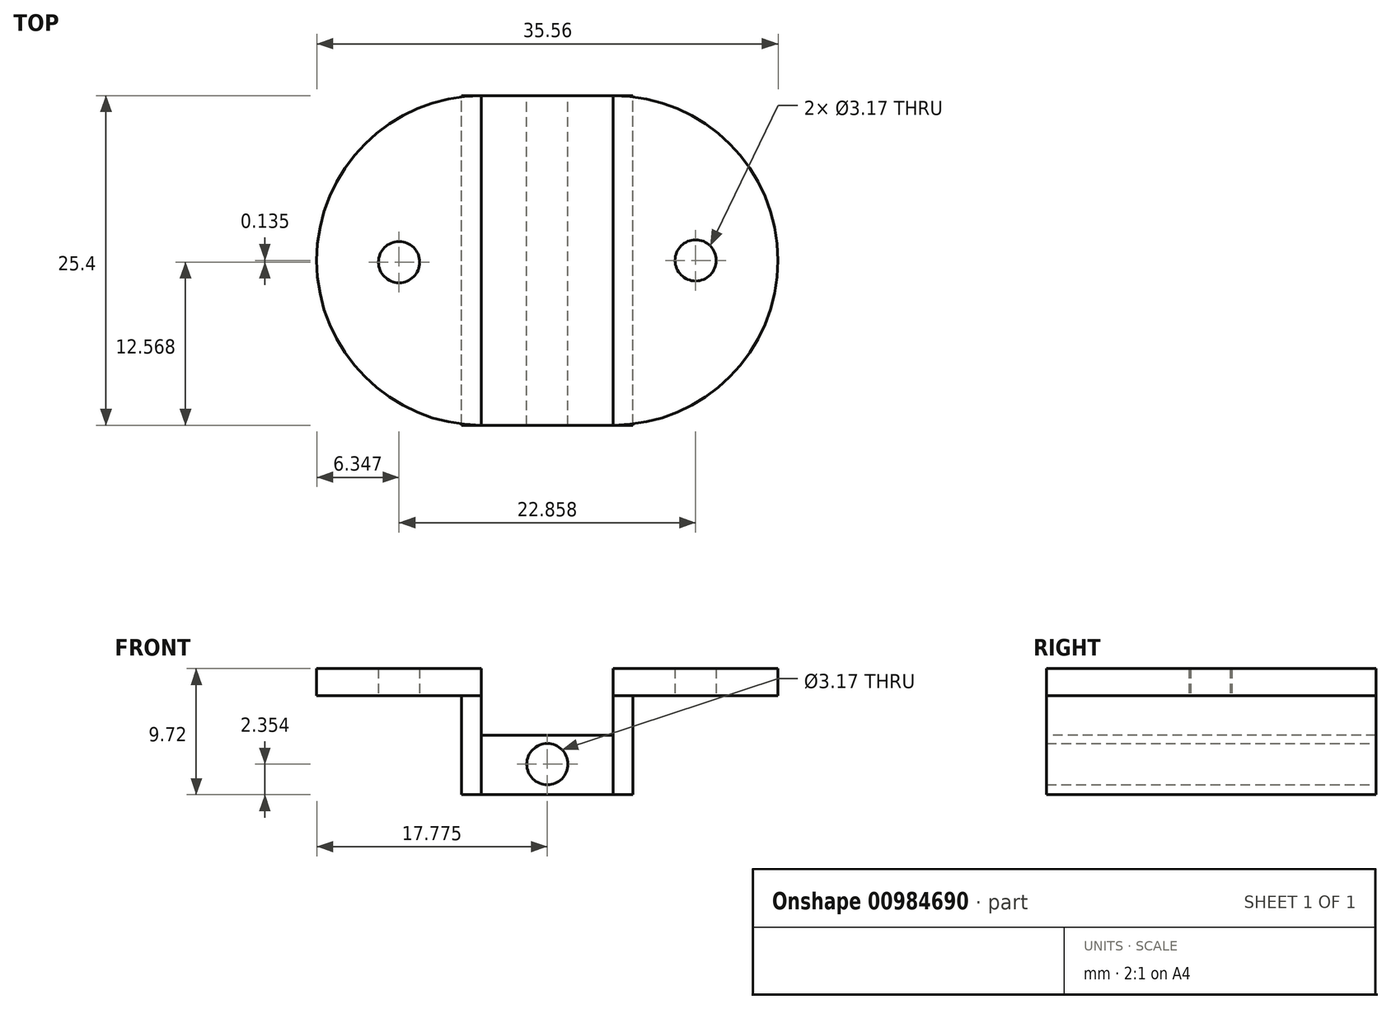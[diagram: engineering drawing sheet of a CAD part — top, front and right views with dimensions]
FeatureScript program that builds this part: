
annotation { "Feature Type Name" : "Feature", "Feature Type Description" : "" }
export const myFeature = defineFeature(function(context is Context, id is Id, definition is map)
    precondition{}
    {
        {
            var Q0;
            Q0=qCreatedBy(makeId("Top.planeOp"),FACE);
            var sketch = newSketch(context, id + "F0", { "sketchPlane" : qUnion([Q0])});
            skLineSegment(sketch, "E0", {"start": v(-48.3, 33.5) * mm, "end": v(-48.3, 8.1) * mm});
            skLineSegment(sketch, "E1", {"start": v(-48.3, 8.1) * mm, "end": v(-48.3, 33.5) * mm});
            skLineSegment(sketch, "E2", {"start": v(-48.3, 33.5) * mm, "end": v(-38.13, 33.5) * mm});
            skLineSegment(sketch, "E3", {"start": v(-38.13, 8.1) * mm, "end": v(-48.3, 8.1) * mm});
            skLineSegment(sketch, "E4", {"start": v(-38.13, 8.1) * mm, "end": v(-38.13, 33.5) * mm});
            skLineSegment(sketch, "E5.bottom", {"start": v(-38.13, 33.5) * mm, "end": v(-36.61, 33.5) * mm});
            skLineSegment(sketch, "E5.top", {"start": v(-38.13, 33.5) * mm, "end": v(-36.61, 33.5) * mm});
            skLineSegment(sketch, "E5.left", {"start": v(-38.13, 33.5) * mm, "end": v(-38.13, 33.5) * mm});
            skLineSegment(sketch, "E5.right", {"start": v(-36.61, 33.5) * mm, "end": v(-36.61, 33.5) * mm});
            skLineSegment(sketch, "E6.bottom", {"start": v(-38.13, 8.1) * mm, "end": v(-36.61, 8.1) * mm});
            skLineSegment(sketch, "E7", {"start": v(-48.3, 33.5) * mm, "end": v(-49.82, 33.5) * mm});
            skLineSegment(sketch, "E8", {"start": v(-48.3, 8.1) * mm, "end": v(-49.82, 8.1) * mm});
            skLineSegment(sketch, "E9", {"start": v(-49.82, 8.1) * mm, "end": v(-49.82, 33.5) * mm});
            skLineSegment(sketch, "E10", {"start": v(-36.61, 8.1) * mm, "end": v(-36.61, 33.5) * mm});
            skLineSegment(sketch, "E11.bottom", {"start": v(-36.61, 8.1) * mm, "end": v(-38.13, 8.1) * mm});
            skLineSegment(sketch, "E11.top", {"start": v(-36.61, 33.5) * mm, "end": v(-38.13, 33.5) * mm});
            skLineSegment(sketch, "E12.bottom", {"start": v(-48.3, 8.1) * mm, "end": v(-38.03, 8.1) * mm});
            skLineSegment(sketch, "E13.bottom", {"start": v(-36.61, 33.5) * mm, "end": v(-21.77, 33.5) * mm});
            skLineSegment(sketch, "E13.top", {"start": v(-36.61, 33.5) * mm, "end": v(-21.77, 33.5) * mm});
            skLineSegment(sketch, "E13.right", {"start": v(-21.77, 33.5) * mm, "end": v(-21.77, 33.5) * mm});
            skLineSegment(sketch, "E14.bottom", {"start": v(-36.61, 8.1) * mm, "end": v(-21.77, 8.1) * mm});
            skLineSegment(sketch, "E14.top", {"start": v(-36.61, 8.1) * mm, "end": v(-21.77, 8.1) * mm});
            skLineSegment(sketch, "E14.left", {"start": v(-36.61, 8.1) * mm, "end": v(-36.61, 8.1) * mm});
            skLineSegment(sketch, "E14.right", {"start": v(-21.77, 8.1) * mm, "end": v(-21.77, 8.1) * mm});
            skLineSegment(sketch, "E15.bottom", {"start": v(-49.82, 8.1) * mm, "end": v(-64.66, 8.1) * mm});
            skLineSegment(sketch, "E15.top", {"start": v(-49.82, 8.1) * mm, "end": v(-64.66, 8.1) * mm});
            skLineSegment(sketch, "E15.left", {"start": v(-49.82, 8.1) * mm, "end": v(-49.82, 8.1) * mm});
            skLineSegment(sketch, "E15.right", {"start": v(-64.66, 8.1) * mm, "end": v(-64.66, 8.1) * mm});
            skLineSegment(sketch, "E16.bottom", {"start": v(-49.82, 33.5) * mm, "end": v(-64.66, 33.5) * mm});
            skLineSegment(sketch, "E16.top", {"start": v(-49.82, 33.5) * mm, "end": v(-64.66, 33.5) * mm});
            skLineSegment(sketch, "E16.left", {"start": v(-49.82, 33.5) * mm, "end": v(-49.82, 33.5) * mm});
            skLineSegment(sketch, "E16.right", {"start": v(-64.66, 33.5) * mm, "end": v(-64.66, 33.5) * mm});
            skLineSegment(sketch, "E17", {"start": v(-64.66, 33.5) * mm, "end": v(-64.66, 8.1) * mm});
            skLineSegment(sketch, "E18", {"start": v(-21.77, 33.5) * mm, "end": v(-21.77, 8.1) * mm});
            skSolve(sketch);
        }
        {
            var Q0;
            Q0=qCreatedBy(makeId("Front.planeOp"),FACE);
            var sketch = newSketch(context, id + "F1", { "sketchPlane" : qUnion([Q0])});
            skSolve(sketch);
        }
        {
            var Q0;
            Q0=makeQuery(id+"F0.imprint","IMPRINT",FACE,{"disambiguationData":[TD([[makeQuery(id+"F0.imprint","IMPRINT",EDGE,{"derivedFrom":sQuery(id+"F0.wireOp",EDGE,"E0")}),1.0]])]});
            extrude(context, id + "F2", {"entities" : qUnion([Q0]), "depth" : 4.57 * mm, "offsetDistance" : 25.4 * mm});
        }
        {
            var Q0;
            Q0=qSketchRegion(id+"F1",true);
            var Q1;
            {var subQ1=sQuery(id+"F0.wireOp",EDGE,"E4");Q1=makeQuery(id+"F0.imprint","IMPRINT",FACE,{"disambiguationData":[TD([[makeQuery(id+"F0.imprint","IMPRINT",EDGE,{"derivedFrom":subQ1}),-1.0]])]});}
            var Q2;
            Q2=makeQuery(id+"F0.imprint","IMPRINT",FACE,{"disambiguationData":[TD([[makeQuery(id+"F0.imprint","IMPRINT",EDGE,{"derivedFrom":sQuery(id+"F0.wireOp",EDGE,"E0")}),-1.0]])]});
            extrude(context, id + "F3", {"entities" : qUnion([Q0, Q1, Q2]), "depth" : 7.62 * mm, "offsetDistance" : 25.4 * mm});
        }
        {
            var Q0;
            Q0=makeQuery(id+"F3.opExtrude","CAP_FACE",FACE,{"disambiguationData":[OSD([sQuery(id+"F0.wireOp",EDGE,"E0"),sQuery(id+"F0.wireOp",EDGE,"E7"),sQuery(id+"F0.wireOp",EDGE,"E8"),sQuery(id+"F0.wireOp",EDGE,"E9")])],"isStart":false});
            var sketch = newSketch(context, id + "F4", { "sketchPlane" : qUnion([Q0])});
            skArc(sketch, "E19", {"start": v(-48.3, 33.5) * mm, "mid": v(-61, 20.8) * mm, "end": v(-48.3, 8.1) * mm});
            skCircle(sketch, "E20", {"center": v(-54.64, 20.67) * mm, "radius": 1.59 * mm});
            skPoint(sketch, "E20.centerSnap0", {"position": v(-59.55, 20.67) * mm});
            skSolve(sketch);
        }
        {
            var Q0;
            Q0=makeQuery(id+"F3.opExtrude","CAP_FACE",FACE,{"disambiguationData":[OSD([sQuery(id+"F0.wireOp",EDGE,"E4"),sQuery(id+"F0.wireOp",EDGE,"E5.bottom"),sQuery(id+"F0.wireOp",EDGE,"E6.bottom"),sQuery(id+"F0.wireOp",EDGE,"E10")])],"isStart":false});
            var sketch = newSketch(context, id + "F5", { "sketchPlane" : qUnion([Q0])});
            skArc(sketch, "E21", {"start": v(-38.13, 8.1) * mm, "mid": v(-25.43, 20.8) * mm, "end": v(-38.13, 33.5) * mm});
            skCircle(sketch, "E22", {"center": v(-31.78, 20.8) * mm, "radius": 1.59 * mm});
            skPoint(sketch, "E22.centerSnap0", {"position": v(-25.43, 20.8) * mm});
            skSolve(sketch);
        }
        {
            var Q0;
            Q0=makeQuery(id+"F4.imprint","IMPRINT",FACE,{"disambiguationData":[TD([[makeQuery(id+"F4.imprint","IMPRINT",EDGE,{"derivedFrom":sQuery(id+"F4.wireOp",EDGE,"E19")}),1.0]])]});
            var Q1;
            Q1=makeQuery(id+"F4.imprint","IMPRINT",FACE,{"disambiguationData":[TD([[makeQuery(id+"F4.imprint","IMPRINT",EDGE,{"derivedFrom":sQuery(id+"F4.wireOp",EDGE,"E20")}),-1.0]])]});
            extrude(context, id + "F6", {"entities" : qUnion([Q0, Q1]), "depth" : 2.1 * mm, "offsetDistance" : 25.4 * mm});
        }
        {
            var Q0;
            Q0=makeQuery(id+"F5.imprint","IMPRINT",FACE,{"disambiguationData":[TD([[makeQuery(id+"F5.imprint","IMPRINT",EDGE,{"derivedFrom":sQuery(id+"F5.wireOp",EDGE,"E21")}),1.0]])]});
            var Q1;
            Q1=makeQuery(id+"F5.imprint","IMPRINT",FACE,{"disambiguationData":[TD([[makeQuery(id+"F5.imprint","IMPRINT",EDGE,{"derivedFrom":sQuery(id+"F5.wireOp",EDGE,"E22")}),-1.0]])]});
            extrude(context, id + "F7", {"entities" : qUnion([Q0, Q1]), "depth" : 2.1 * mm, "offsetDistance" : 25.4 * mm});
        }
        {
            var Q0;
            Q0=makeQuery(id+"F2.opExtrude","SWEPT_FACE",FACE,{"disambiguationData":[OSD([sQuery(id+"F0.wireOp",EDGE,"E2")])]});
            var sketch = newSketch(context, id + "F8", { "sketchPlane" : qUnion([Q0])});
            skCircle(sketch, "E23", {"center": v(43.21, 2.35) * mm, "radius": 1.59 * mm});
            skSolve(sketch);
        }
        {
            var Q0;
            Q0=makeQuery(id+"F8.imprint","IMPRINT",FACE,{"disambiguationData":[TD([[makeQuery(id+"F8.imprint","IMPRINT",EDGE,{"derivedFrom":sQuery(id+"F8.wireOp",EDGE,"E23")}),1.0]])]});
            extrude(context, id + "F9", {"entities" : qUnion([Q0]), "operationType" : NewBodyOperationType.REMOVE, "oppositeDirection" : true, "depth" : 25.4 * mm, "offsetDistance" : 25.4 * mm});
        }
    });
